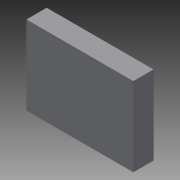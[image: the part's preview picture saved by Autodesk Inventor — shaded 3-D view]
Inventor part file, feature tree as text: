
AUTODESK INVENTOR PART (.ipt)
format: ipt  version: 2014 (Build 180170000, 170)  size: 68,096 bytes
history: native  units: mm
features: extrude x1, sketch x1
ambient origin geometry x8: Origin, YZ Plane, XZ Plane, XY Plane, X Axis, Y Axis, Z Axis, Center Point
bodies: Solid1 (feature_tree)
feature tree (2):
  extrude  "Extrusion1"  Depth=111.0mm
  sketch  "Sketch1"  dims[d0=21.0mm d1=0.0mm d2=111.0mm d3=82.0mm]
